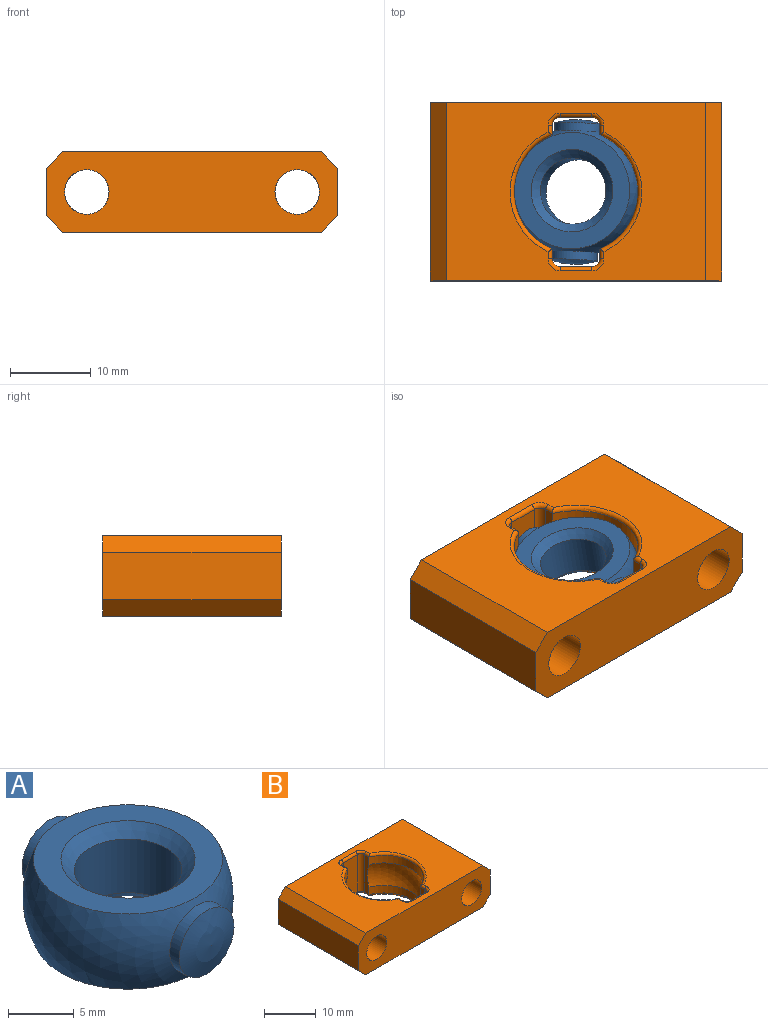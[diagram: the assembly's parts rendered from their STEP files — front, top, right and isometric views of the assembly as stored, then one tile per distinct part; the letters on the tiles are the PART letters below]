
ASSEMBLY  parts=2 mates=1
PART A: 10 faces, bbox 16x17.9x16 mm
  f0: sphere r=8mm, area 295.2mm2, adj f1,f2,f3,f4
  f1: cylinder r=2.95mm len=5.9mm, axis (0,1,0), area 18.8mm2, adj f0,f6
  f2: cylinder r=2.95mm len=5.9mm, axis (0,1,0), area 18.8mm2, adj f0,f5
  f3: plane 14.39x14.39mm, normal (0,0,1), area 80.9mm2, adj f0,f9
  f4: plane 14.39x14.39mm, normal (0,0,-1), area 80.9mm2, adj f0,f8
  f5: sphere r=8.95mm, area 28.1mm2, adj f2
  f6: sphere r=8.95mm, area 28.1mm2, adj f1
  f7: cylinder r=4.1mm len=8.2mm, axis (0,0,1), area 128.8mm2, adj f8,f9
  f8: cone r=4.1mm half-angle=45deg, axis (0,0,-1), area 40.9mm2, adj f4,f7
  f9: cone r=4.1mm half-angle=45deg, axis (0,0,1), area 40.9mm2, adj f3,f7
PART B: 52 faces, bbox 36x22x10.9 mm
  f0: cylinder r=7.65mm len=14.12mm, axis (0,0,-1), area 32.1mm2, adj f13,f14,f19,f29
  f1: cylinder r=7.65mm len=14.12mm, axis (0,0,-1), area 32.1mm2, adj f5,f18,f20,f38
  f2: cylinder r=7.65mm len=14.12mm, axis (0,0,-1), area 32.1mm2, adj f13,f14,f19,f47
  f3: cylinder r=7.65mm len=14.12mm, axis (0,0,-1), area 32.1mm2, adj f5,f18,f20,f44
  f4: plane 32x22mm, normal (0,0,1), area 471.7mm2, adj f6,f8,f25,f27,f40,f41,f42,f43
  f5: sphere r=8.1mm, area 102.7mm2, adj f1,f3,f18,f20
  f6: plane 36x9.9mm, normal (0,1,0), area 300.9mm2, adj f4,f7,f9,f10,f11,f12,f24,f25
  f7: plane 22x5.9mm, normal (-1,0,0), area 129.8mm2, adj f6,f8,f26,f27
  f8: plane 36x9.9mm, normal (0,-1,0), area 300.9mm2, adj f4,f7,f9,f10,f11,f12,f24,f25
  f9: plane 22x5.9mm, normal (1,0,0), area 129.8mm2, adj f6,f8,f24,f25
  f10: plane 32x22mm, normal (0,0,-1), area 471.7mm2, adj f6,f8,f24,f26,f28,f29,f30,f31
  f11: cylinder r=2.75mm len=22mm, axis (0,-1,0), area 380.1mm2, adj f6,f8
  f12: cylinder r=2.75mm len=22mm, axis (0,-1,0), area 380.1mm2, adj f6,f8
  f13: sphere r=8.1mm, area 102.7mm2, adj f0,f2,f14,f19
  f14: plane 8.9x1.19mm, normal (1,0,0), area 8.9mm2, adj f0,f2,f13,f15,f31,f49
  f15: cylinder r=1mm len=8.9mm, axis (0,0,1), area 14mm2, adj f14,f16,f33,f51
  f16: plane 8.9x3.9mm, normal (0,1,0), area 34.7mm2, adj f15,f17,f35,f50
  f17: cylinder r=1mm len=8.9mm, axis (0,0,1), area 14mm2, adj f16,f18,f37,f48
  f18: plane 8.9x1.19mm, normal (-1,0,0), area 8.9mm2, adj f1,f3,f5,f17,f39,f46
  f19: plane 8.9x1.19mm, normal (1,0,0), area 8.9mm2, adj f0,f2,f13,f21,f28,f45
  f20: plane 8.9x1.19mm, normal (-1,0,0), area 8.9mm2, adj f1,f3,f5,f22,f36,f42
  f21: cylinder r=1mm len=8.9mm, axis (0,0,1), area 14mm2, adj f19,f23,f30,f43
  f22: cylinder r=1mm len=8.9mm, axis (0,0,1), area 14mm2, adj f20,f23,f34,f40
  f23: plane 8.9x3.9mm, normal (0,-1,0), area 34.7mm2, adj f21,f22,f32,f41
  f24: plane 22x2mm, normal (0.71,0,-0.71), area 62.2mm2, adj f6,f8,f9,f10
  f25: plane 22x2mm, normal (0.71,0,0.71), area 62.2mm2, adj f4,f6,f8,f9
  f26: plane 22x2mm, normal (-0.71,0,-0.71), area 62.2mm2, adj f6,f7,f8,f10
  f27: plane 22x2mm, normal (-0.71,0,0.71), area 62.2mm2, adj f4,f6,f7,f8
  f28: cylinder r=0.5mm len=1.19mm, axis (0,1,0), area 0.8mm2, adj f10,f19,f29,f30
  f29: torus R=8.15mm, axis (0,0,1), area 14.3mm2, adj f0,f10,f28,f31
  f30: torus R=1.5mm, axis (0,0,1), area 1.5mm2, adj f10,f21,f28,f32
  f31: cylinder r=0.5mm len=1.19mm, axis (0,1,0), area 0.8mm2, adj f10,f14,f29,f33
  f32: cylinder r=0.5mm len=3.9mm, axis (1,0,0), area 3.1mm2, adj f10,f23,f30,f34
  f33: torus R=1.5mm, axis (0,0,1), area 1.5mm2, adj f10,f15,f31,f35
  f34: torus R=1.5mm, axis (0,0,1), area 1.5mm2, adj f10,f22,f32,f36
  f35: cylinder r=0.5mm len=3.9mm, axis (-1,0,0), area 3.1mm2, adj f10,f16,f33,f37
  f36: cylinder r=0.5mm len=1.19mm, axis (0,-1,0), area 0.8mm2, adj f10,f20,f34,f38
  f37: torus R=1.5mm, axis (0,0,1), area 1.5mm2, adj f10,f17,f35,f39
  f38: torus R=8.15mm, axis (0,0,1), area 14.3mm2, adj f1,f10,f36,f39
  f39: cylinder r=0.5mm len=1.19mm, axis (0,-1,0), area 0.8mm2, adj f10,f18,f37,f38
  f40: torus R=1.5mm, axis (0,0,1), area 1.5mm2, adj f4,f22,f41,f42
  f41: cylinder r=0.5mm len=3.9mm, axis (1,0,0), area 3.1mm2, adj f4,f23,f40,f43
  f42: cylinder r=0.5mm len=1.19mm, axis (0,-1,0), area 0.8mm2, adj f4,f20,f40,f44
  f43: torus R=1.5mm, axis (0,0,1), area 1.5mm2, adj f4,f21,f41,f45
  f44: torus R=8.15mm, axis (0,0,1), area 14.3mm2, adj f3,f4,f42,f46
  f45: cylinder r=0.5mm len=1.19mm, axis (0,1,0), area 0.8mm2, adj f4,f19,f43,f47
  f46: cylinder r=0.5mm len=1.19mm, axis (0,-1,0), area 0.8mm2, adj f4,f18,f44,f48
  f47: torus R=8.15mm, axis (0,0,1), area 14.3mm2, adj f2,f4,f45,f49
  f48: torus R=1.5mm, axis (0,0,1), area 1.5mm2, adj f4,f17,f46,f50
  f49: cylinder r=0.5mm len=1.19mm, axis (0,1,0), area 0.8mm2, adj f4,f14,f47,f51
  f50: cylinder r=0.5mm len=3.9mm, axis (-1,0,0), area 3.1mm2, adj f4,f16,f48,f51
  f51: torus R=1.5mm, axis (0,0,1), area 1.5mm2, adj f4,f15,f49,f50
PLACE A rot(axis=(-0.29,-0.92,-0.25),8.8deg) t=(-21.57,-3.23,9.05)mm
PLACE B t=(-22.26,-3,8.99)mm fixed
MATE ball A.f7 <-> B.f0  axis (-0.14,0.05,0.99) through (-22.26,-3,13.94)mm
